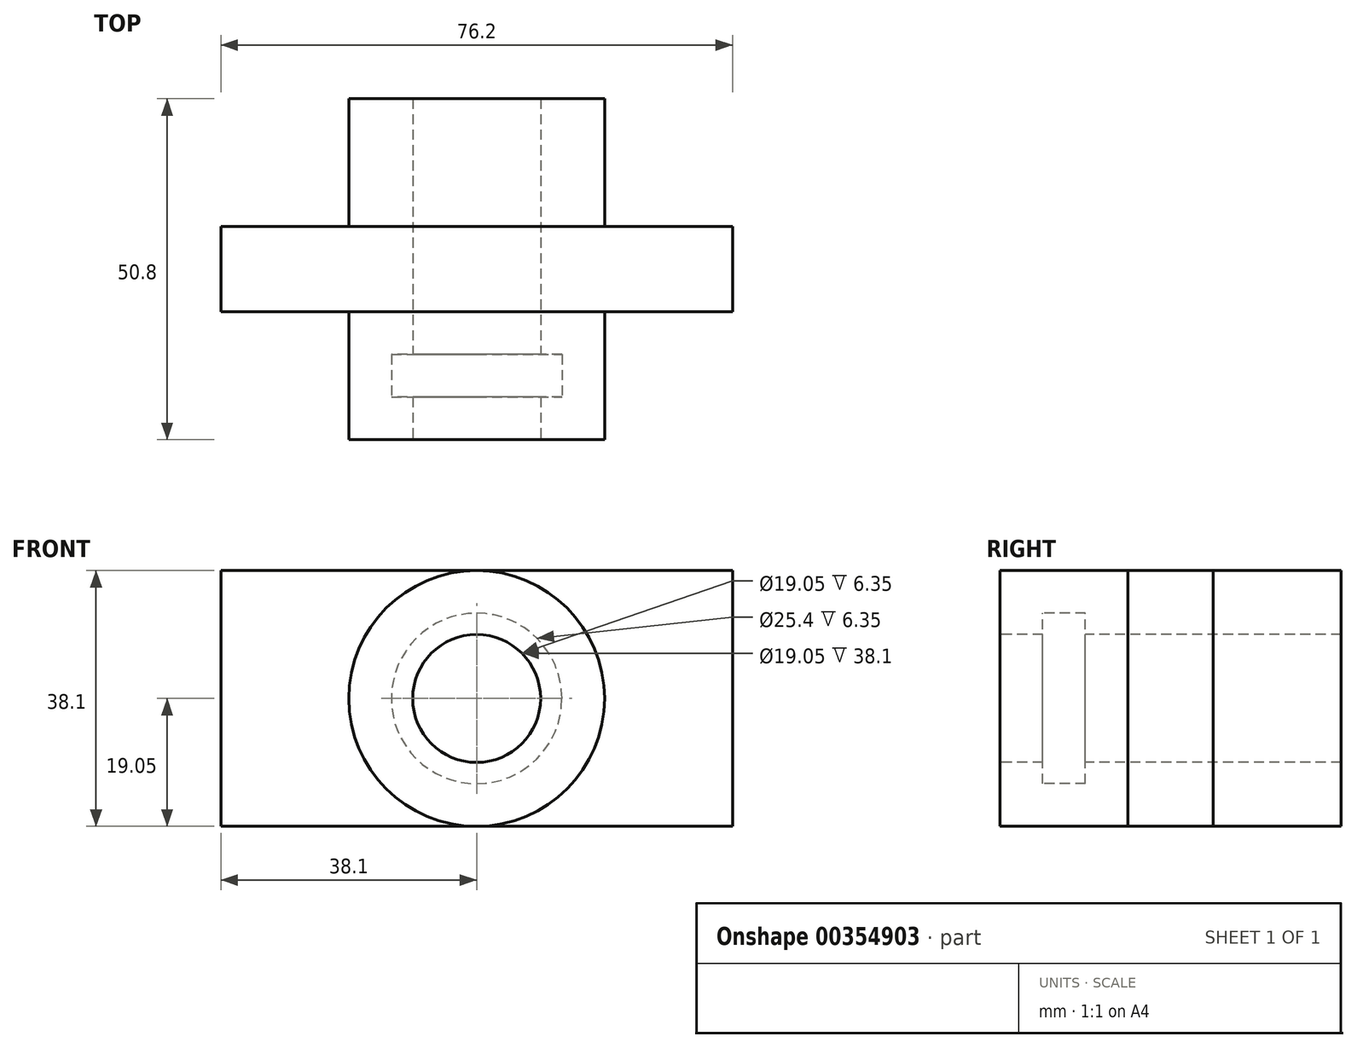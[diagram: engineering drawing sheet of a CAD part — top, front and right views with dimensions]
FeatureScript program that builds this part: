
annotation { "Feature Type Name" : "Feature", "Feature Type Description" : "" }
export const myFeature = defineFeature(function(context is Context, id is Id, definition is map)
    precondition{}
    {
        {
            var Q0;
            Q0=qCreatedBy(makeId("Front.planeOp"),FACE);
            var sketch = newSketch(context, id + "F0", { "sketchPlane" : qUnion([Q0])});
            skLineSegment(sketch, "E0.bottom", {"start": v(0, 0) * mm, "end": v(76.2, 0) * mm});
            skLineSegment(sketch, "E0.top", {"start": v(0, 38.1) * mm, "end": v(76.2, 38.1) * mm});
            skLineSegment(sketch, "E0.left", {"start": v(0, 0) * mm, "end": v(0, 38.1) * mm});
            skLineSegment(sketch, "E0.right", {"start": v(76.2, 0) * mm, "end": v(76.2, 38.1) * mm});
            skCircle(sketch, "E1", {"center": v(38.1, 19.05) * mm, "radius": 19.05 * mm});
            skPoint(sketch, "E1.centerSnap0", {"position": v(0, 19.05) * mm});
            skPoint(sketch, "E1.centerSnap1", {"position": v(38.1, 38.1) * mm});
            skCircle(sketch, "E2", {"center": v(38.1, 19.05) * mm, "radius": 9.53 * mm});
            skCircle(sketch, "E3", {"center": v(38.1, 19.05) * mm, "radius": 12.7 * mm, "construction": true});
            skSolve(sketch);
        }
        {
            var Q0;
            Q0=makeQuery(id+"F0.imprint","IMPRINT",FACE,{"disambiguationData":[TD([[makeQuery(id+"F0.imprint","IMPRINT",EDGE,{"derivedFrom":sQuery(id+"F0.wireOp",EDGE,"E2")}),-1.0]])]});
            var Q1;
            Q1=makeQuery(id+"F0.imprint","IMPRINT",FACE,{"disambiguationData":[TD([[makeQuery(id+"F0.imprint","IMPRINT",EDGE,{"derivedFrom":sQuery(id+"F0.wireOp",EDGE,"E2")}),1.0]])]});
            extrude(context, id + "F1", {"entities" : qUnion([Q0, Q1]), "endBound" : BoundingType.SYMMETRIC, "depth" : 50.8 * mm});
        }
        {
            var Q0;
            Q0=makeQuery(id+"F1.opExtrude","CAP_FACE",FACE,{"disambiguationData":[OSD([sQuery(id+"F0.wireOp",EDGE,"E1")])],"isStart":false});
            var sketch = newSketch(context, id + "F2", { "sketchPlane" : qUnion([Q0])});
            skCircle(sketch, "E4", {"center": v(38.1, 19.05) * mm, "radius": 9.53 * mm});
            skSolve(sketch);
        }
        {
            var Q0;
            Q0 = qSketchRegion(id + "F2", true);
            extrude(context, id + "F3", {"entities" : qUnion([Q0]), "operationType" : NewBodyOperationType.REMOVE, "oppositeDirection" : true, "depth" : 6.35 * mm});
        }
        {
            var Q0;
            Q0=makeQuery(id+"F3.boolean.opBoolean","COPY",FACE,{"derivedFrom":makeQuery(id+"F3.opExtrude","CAP_FACE",FACE,{"disambiguationData":[OSD([sQuery(id+"F2.wireOp",EDGE,"E4")])],"isStart":false})});
            var sketch = newSketch(context, id + "F4", { "sketchPlane" : qUnion([Q0])});
            skCircle(sketch, "E5", {"center": v(38.1, 19.05) * mm, "radius": 12.7 * mm});
            skSolve(sketch);
        }
        {
            var Q0;
            Q0 = qSketchRegion(id + "F4", true);
            extrude(context, id + "F5", {"entities" : qUnion([Q0]), "operationType" : NewBodyOperationType.REMOVE, "oppositeDirection" : true, "depth" : 6.35 * mm});
        }
        {
            var Q0;
            Q0=makeQuery(id+"F5.boolean.opBoolean","COPY",FACE,{"derivedFrom":makeQuery(id+"F5.opExtrude","CAP_FACE",FACE,{"disambiguationData":[OSD([sQuery(id+"F4.wireOp",EDGE,"E5")])],"isStart":false})});
            var sketch = newSketch(context, id + "F6", { "sketchPlane" : qUnion([Q0])});
            skCircle(sketch, "E6", {"center": v(38.1, 19.05) * mm, "radius": 9.53 * mm});
            skSolve(sketch);
        }
        {
            var Q0;
            Q0 = qSketchRegion(id + "F6", true);
            extrude(context, id + "F7", {"entities" : qUnion([Q0]), "operationType" : NewBodyOperationType.REMOVE, "oppositeDirection" : true, "depth" : 76.2 * mm});
        }
        {
            var Q0;
            {var subQ0=sQuery(id+"F0.wireOp",EDGE,"E0.left");Q0=makeQuery(id+"F0.imprint","IMPRINT",FACE,{"disambiguationData":[TD([[makeQuery(id+"F0.imprint","IMPRINT",EDGE,{"derivedFrom":subQ0}),-1.0]])]});}
            var Q1;
            {var subQ0=sQuery(id+"F0.wireOp",EDGE,"E0.right");Q1=makeQuery(id+"F0.imprint","IMPRINT",FACE,{"disambiguationData":[TD([[makeQuery(id+"F0.imprint","IMPRINT",EDGE,{"derivedFrom":subQ0}),1.0]])]});}
            extrude(context, id + "F8", {"entities" : qUnion([Q0, Q1]), "operationType" : NewBodyOperationType.ADD, "endBound" : BoundingType.SYMMETRIC, "depth" : 12.7 * mm});
        }
    });
